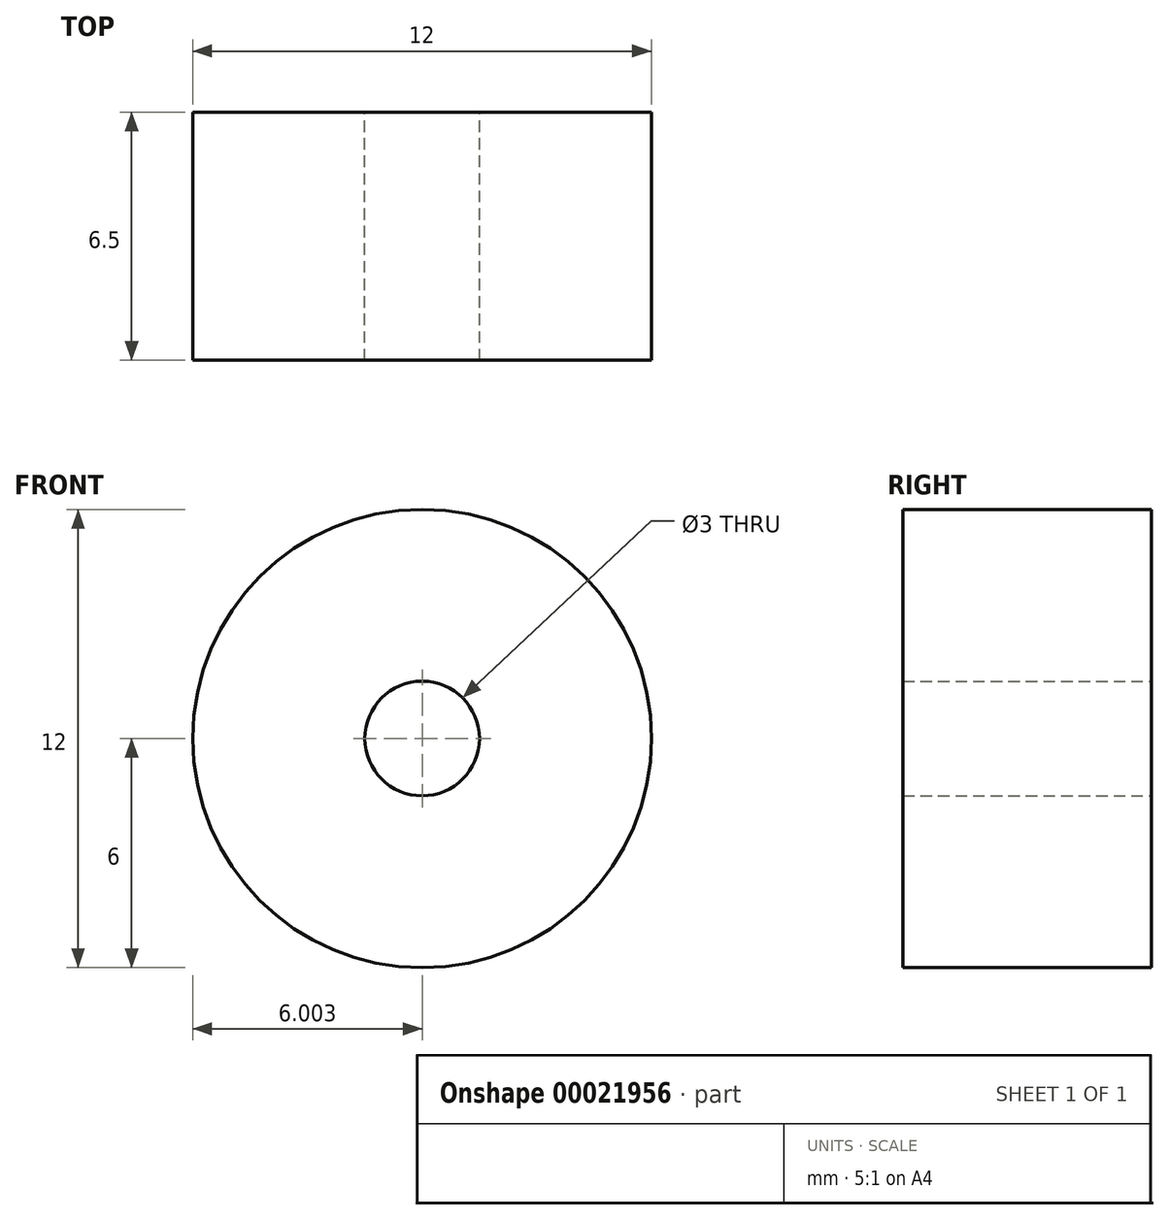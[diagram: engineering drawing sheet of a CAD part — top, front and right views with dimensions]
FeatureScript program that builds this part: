
annotation { "Feature Type Name" : "Feature", "Feature Type Description" : "" }
export const myFeature = defineFeature(function(context is Context, id is Id, definition is map)
    precondition{}
    {
        {
            var Q0;
            Q0=qCreatedBy(makeId("Front.planeOp"),FACE);
            var sketch = newSketch(context, id + "F0", { "sketchPlane" : qUnion([Q0])});
            skCircle(sketch, "E0", {"center": v(36.65, 26.67) * mm, "radius": 6 * mm});
            skCircle(sketch, "E1", {"center": v(36.65, 26.67) * mm, "radius": 1.5 * mm});
            skSolve(sketch);
        }
        {
            var Q0;
            Q0=qSketchRegion(id+"F0",true);
            var Q1;
            Q1=makeQuery(id+"F0.imprint","IMPRINT",FACE,{"disambiguationData":[TD([[makeQuery(id+"F0.imprint","IMPRINT",EDGE,{"derivedFrom":sQuery(id+"F0.wireOp",EDGE,"E0")}),1.0]])]});
            extrude(context, id + "F1", {"entities" : qUnion([Q0, Q1]), "depth" : 6.5 * mm});
        }
    });
